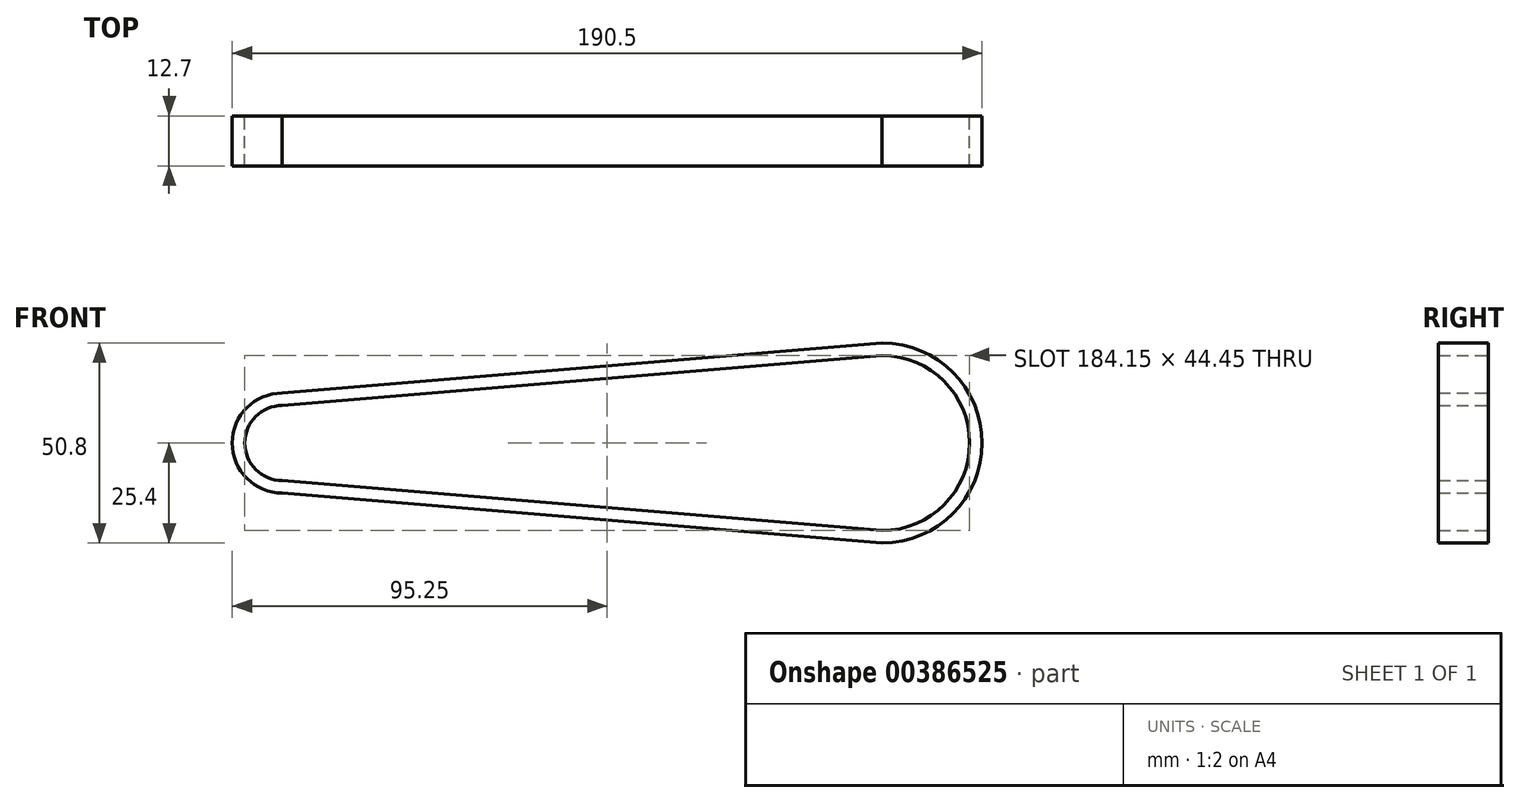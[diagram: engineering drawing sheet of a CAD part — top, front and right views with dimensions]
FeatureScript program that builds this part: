
annotation { "Feature Type Name" : "Feature", "Feature Type Description" : "" }
export const myFeature = defineFeature(function(context is Context, id is Id, definition is map)
    precondition{}
    {
        {
            var Q0;
            Q0=qCreatedBy(makeId("Front.planeOp"),FACE);
            var sketch = newSketch(context, id + "F0", { "sketchPlane" : qUnion([Q0])});
            skArc(sketch, "E0", {"start": v(0, 12.7) * mm, "mid": v(-12.7, 0) * mm, "end": v(0, -12.7) * mm});
            skArc(sketch, "E1", {"start": v(0, 9.53) * mm, "mid": v(-9.53, 0) * mm, "end": v(0, -9.53) * mm});
            skArc(sketch, "E2", {"start": v(152.4, -25.4) * mm, "mid": v(177.8, 0) * mm, "end": v(152.4, 25.4) * mm});
            skArc(sketch, "E3", {"start": v(152.4, -22.23) * mm, "mid": v(174.62, 0) * mm, "end": v(152.4, 22.23) * mm});
            skLineSegment(sketch, "E4", {"start": v(0, 12.7) * mm, "end": v(152.4, 25.4) * mm});
            skLineSegment(sketch, "E5", {"start": v(0, -12.7) * mm, "end": v(152.4, -25.4) * mm});
            skLineSegment(sketch, "E6", {"start": v(0, 9.52) * mm, "end": v(152.4, 22.23) * mm});
            skLineSegment(sketch, "E7", {"start": v(0, -9.52) * mm, "end": v(152.4, -22.23) * mm});
            skSolve(sketch);
        }
        {
            var Q0;
            Q0 = qSketchRegion(id + "F0", true);
            extrude(context, id + "F1", {"entities" : qUnion([Q0]), "depth" : 12.7 * mm});
        }
    });
